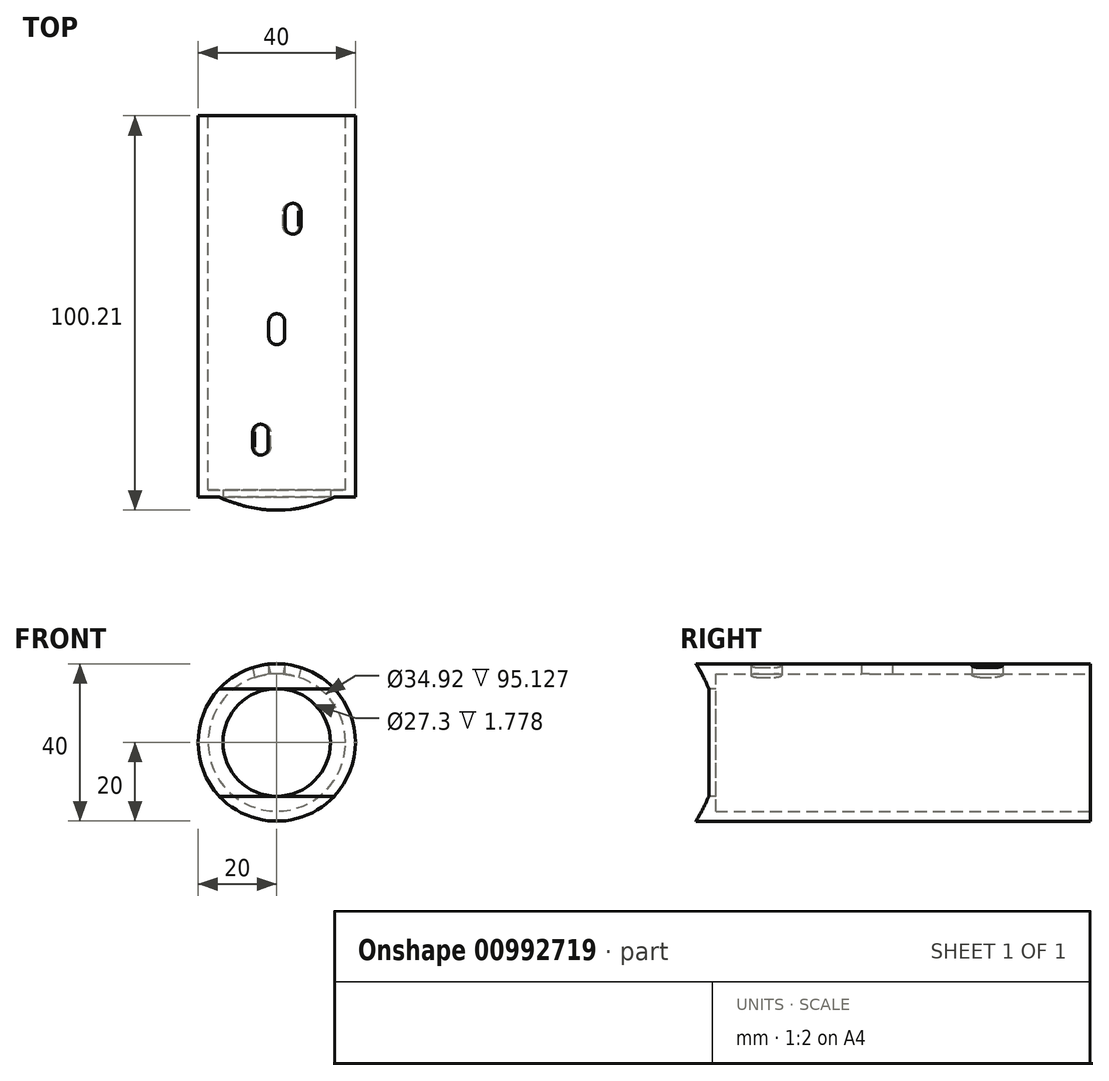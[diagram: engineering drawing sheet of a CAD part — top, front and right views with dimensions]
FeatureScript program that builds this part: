
annotation { "Feature Type Name" : "Feature", "Feature Type Description" : "" }
export const myFeature = defineFeature(function(context is Context, id is Id, definition is map)
    precondition{}
    {
        {
            var Q0;
            Q0=qCreatedBy(makeId("Front.planeOp"),FACE);
            var sketch = newSketch(context, id + "F0", { "sketchPlane" : qUnion([Q0])});
            skCircle(sketch, "E0", {"center": v(0, 0) * mm, "radius": 20 * mm});
            skCircle(sketch, "E1", {"center": v(0, 0) * mm, "radius": 17.46 * mm});
            skSolve(sketch);
        }
        {
            var Q0;
            Q0=qSketchRegion(id+"F0",true);
            extrude(context, id + "F1", {"entities" : qUnion([Q0]), "endBound" : BoundingType.SYMMETRIC, "depth" : 95 * mm, "offsetDistance" : 25.4 * mm});
        }
        {
            var Q0;
            Q0=makeQuery(id+"F1.opExtrude","CAP_FACE",FACE,{"disambiguationData":[OSD([sQuery(id+"F0.wireOp",EDGE,"E0"),sQuery(id+"F0.wireOp",EDGE,"E1")])],"isStart":false});
            var sketch = newSketch(context, id + "F2", { "sketchPlane" : qUnion([Q0])});
            skCircle(sketch, "E2", {"center": v(0, 0) * mm, "radius": 13.65 * mm});
            skCircle(sketch, "E3.0", {"center": v(0, 0) * mm, "radius": 20 * mm});
            skCircle(sketch, "E4.0", {"center": v(0, 0) * mm, "radius": 17.46 * mm, "construction": true});
            skSolve(sketch);
        }
        {
            var Q0;
            Q0=qSketchRegion(id+"F2",true);
            extrude(context, id + "F3", {"entities" : qUnion([Q0]), "operationType" : NewBodyOperationType.ADD, "oppositeDirection" : true, "depth" : 5.08 * mm, "offsetDistance" : 25.4 * mm});
        }
        {
            var Q0;
            Q0=qCreatedBy(makeId("Right.planeOp"),FACE);
            var sketch = newSketch(context, id + "F4", { "sketchPlane" : qUnion([Q0])});
            skLineSegment(sketch, "E5.0", {"start": v(-47.5, -20) * mm, "end": v(-47.5, -20) * mm});
            skArc(sketch, "E6", {"start": v(-44.2, 13.65) * mm, "mid": v(-45.7, 16.9) * mm, "end": v(-47.5, 20) * mm});
            skLineSegment(sketch, "E7.0", {"start": v(-42.42, -17.46) * mm, "end": v(-42.42, 17.46) * mm, "construction": true});
            skLineSegment(sketch, "E8", {"start": v(-42.42, 13.65) * mm, "end": v(-44.2, 13.65) * mm, "construction": true});
            skLineSegment(sketch, "E9", {"start": v(-44.2, 13.65) * mm, "end": v(-44.2, -13.65) * mm});
            skArc(sketch, "E10", {"start": v(-47.5, 20) * mm, "mid": v(-114.68, -3.58) * mm, "end": v(-44.2, -13.65) * mm, "construction": true});
            skLineSegment(sketch, "E11", {"start": v(-47.5, -20) * mm, "end": v(-47.5, 20) * mm});
            skArc(sketch, "E12.MirrorCS", {"start": v(-44.2, -13.65) * mm, "mid": v(-45.7, -16.9) * mm, "end": v(-47.5, -20) * mm});
            skSolve(sketch);
        }
        {
            var Q0;
            Q0=qSketchRegion(id+"F4",true);
            extrude(context, id + "F5", {"entities" : qUnion([Q0]), "operationType" : NewBodyOperationType.REMOVE, "endBound" : BoundingType.THROUGH_ALL, "oppositeDirection" : true, "depth" : 25.4 * mm, "offsetDistance" : 25.4 * mm, "hasSecondDirection" : true, "secondDirectionBound" : SecondDirectionBoundingType.THROUGH_ALL, "secondDirectionOppositeDirection" : false, "secondDirectionDepth" : 25.4 * mm});
        }
        {
            var Q0;
            Q0=qCreatedBy(makeId("Top.planeOp"),FACE);
            var sketch = newSketch(context, id + "F6", { "sketchPlane" : qUnion([Q0])});
            skLineSegment(sketch, "E13.bottom", {"start": v(-2.03, -3.43) * mm, "end": v(2.03, -3.43) * mm, "construction": true});
            skLineSegment(sketch, "E13.top", {"start": v(-2.03, 0.38) * mm, "end": v(2.03, 0.38) * mm, "construction": true});
            skLineSegment(sketch, "E13.left", {"start": v(-2.03, -3.43) * mm, "end": v(-2.03, 0.38) * mm});
            skLineSegment(sketch, "E13.right", {"start": v(2.03, -3.43) * mm, "end": v(2.03, 0.38) * mm});
            skArc(sketch, "E14", {"start": v(-2.03, 0.38) * mm, "mid": v(0, 2.41) * mm, "end": v(2.03, 0.38) * mm});
            skArc(sketch, "E15", {"start": v(-2.03, -3.43) * mm, "mid": v(0, -5.46) * mm, "end": v(2.03, -3.43) * mm});
            skSolve(sketch);
        }
        {
            var Q0;
            Q0=qSketchRegion(id+"F6",true);
            extrude(context, id + "F7", {"entities" : qUnion([Q0]), "operationType" : NewBodyOperationType.REMOVE, "endBound" : BoundingType.THROUGH_ALL, "depth" : 25.4 * mm, "offsetDistance" : 25.4 * mm});
        }
        {
            var Q0;
            Q0=qCreatedBy(makeId("Front.planeOp"),FACE);
            var sketch = newSketch(context, id + "F8", { "sketchPlane" : qUnion([Q0])});
            skLineSegment(sketch, "E16", {"start": v(-43.88, 9.33) * mm, "end": v(0, 0) * mm, "construction": true});
            skLineSegment(sketch, "E17", {"start": v(0, 0) * mm, "end": v(39.67, 8.43) * mm, "construction": true});
            skSolve(sketch);
        }
        {
            var Q0;
            Q0=sQuery(id+"F8.wireOp",EDGE,"E17");
            var Q1;
            Q1=qCreatedBy(makeId("Top.planeOp"),FACE);
            cPlane(context, id + "F9", {"entities" : qUnion([Q0, Q1]), "cplaneType" : CPlaneType.LINE_ANGLE, "offset" : 25.4 * mm, "angle" : 0 * degree, "width" : 152.4 * mm, "height" : 152.4 * mm});
        }
        {
            var Q0;
            Q0=qCreatedBy(id+"F9.planeOp",FACE);
            var sketch = newSketch(context, id + "F10", { "sketchPlane" : qUnion([Q0])});
            skLineSegment(sketch, "E18.bottom", {"start": v(-2.03, 31.5) * mm, "end": v(2.03, 31.5) * mm, "construction": true});
            skLineSegment(sketch, "E18.top", {"start": v(-2.03, 27.69) * mm, "end": v(2.03, 27.69) * mm, "construction": true});
            skLineSegment(sketch, "E18.left", {"start": v(-2.03, 31.5) * mm, "end": v(-2.03, 27.69) * mm});
            skLineSegment(sketch, "E18.right", {"start": v(2.03, 31.5) * mm, "end": v(2.03, 27.69) * mm});
            skArc(sketch, "E19", {"start": v(-2.03, 27.69) * mm, "mid": v(0, 25.66) * mm, "end": v(2.03, 27.69) * mm});
            skArc(sketch, "E20", {"start": v(-2.03, 31.5) * mm, "mid": v(0, 33.53) * mm, "end": v(2.03, 31.5) * mm});
            skSolve(sketch);
        }
        {
            var Q0;
            Q0=qSketchRegion(id+"F10",true);
            extrude(context, id + "F11", {"entities" : qUnion([Q0]), "operationType" : NewBodyOperationType.REMOVE, "endBound" : BoundingType.THROUGH_ALL, "oppositeDirection" : true, "depth" : 25.4 * mm, "offsetDistance" : 25.4 * mm});
        }
        {
            var Q0;
            Q0=sQuery(id+"F8.wireOp",EDGE,"E16");
            var Q1;
            Q1=qCreatedBy(makeId("Top.planeOp"),FACE);
            cPlane(context, id + "F12", {"entities" : qUnion([Q0, Q1]), "cplaneType" : CPlaneType.LINE_ANGLE, "offset" : 25.4 * mm, "angle" : 0 * degree, "width" : 152.4 * mm, "height" : 152.4 * mm});
        }
        {
            var Q0;
            Q0=qCreatedBy(id+"F12.planeOp",FACE);
            var sketch = newSketch(context, id + "F13", { "sketchPlane" : qUnion([Q0])});
            skLineSegment(sketch, "E21.bottom", {"start": v(2.03, -24.64) * mm, "end": v(-2.03, -24.64) * mm, "construction": true});
            skLineSegment(sketch, "E21.top", {"start": v(2.03, -28.45) * mm, "end": v(-2.03, -28.45) * mm, "construction": true});
            skLineSegment(sketch, "E21.left", {"start": v(2.03, -24.64) * mm, "end": v(2.03, -28.45) * mm});
            skLineSegment(sketch, "E21.right", {"start": v(-2.03, -24.64) * mm, "end": v(-2.03, -28.45) * mm});
            skArc(sketch, "E22", {"start": v(2.03, -24.64) * mm, "mid": v(0, -22.6) * mm, "end": v(-2.03, -24.64) * mm});
            skArc(sketch, "E23", {"start": v(2.03, -28.45) * mm, "mid": v(0, -30.48) * mm, "end": v(-2.03, -28.45) * mm});
            skSolve(sketch);
        }
        {
            var Q0;
            Q0=qSketchRegion(id+"F13",true);
            extrude(context, id + "F14", {"entities" : qUnion([Q0]), "operationType" : NewBodyOperationType.REMOVE, "endBound" : BoundingType.THROUGH_ALL, "oppositeDirection" : true, "depth" : 25.4 * mm, "offsetDistance" : 25.4 * mm});
        }
        {
            var Q0;
            Q0=makeQuery(id+"F1.opExtrude","CAP_FACE",FACE,{"disambiguationData":[OSD([sQuery(id+"F0.wireOp",EDGE,"E0"),sQuery(id+"F0.wireOp",EDGE,"E1")])],"isStart":true});
            var sketch = newSketch(context, id + "F15", { "sketchPlane" : qUnion([Q0])});
            skCircle(sketch, "E24.0", {"center": v(0, 0) * mm, "radius": 20 * mm});
            skCircle(sketch, "E25.0", {"center": v(0, 0) * mm, "radius": 17.46 * mm});
            skSolve(sketch);
        }
        {
            var Q0;
            Q0=qSketchRegion(id+"F15",true);
            extrude(context, id + "F16", {"entities" : qUnion([Q0]), "operationType" : NewBodyOperationType.ADD, "depth" : 5.2 * mm, "offsetDistance" : 25.4 * mm});
        }
    });
